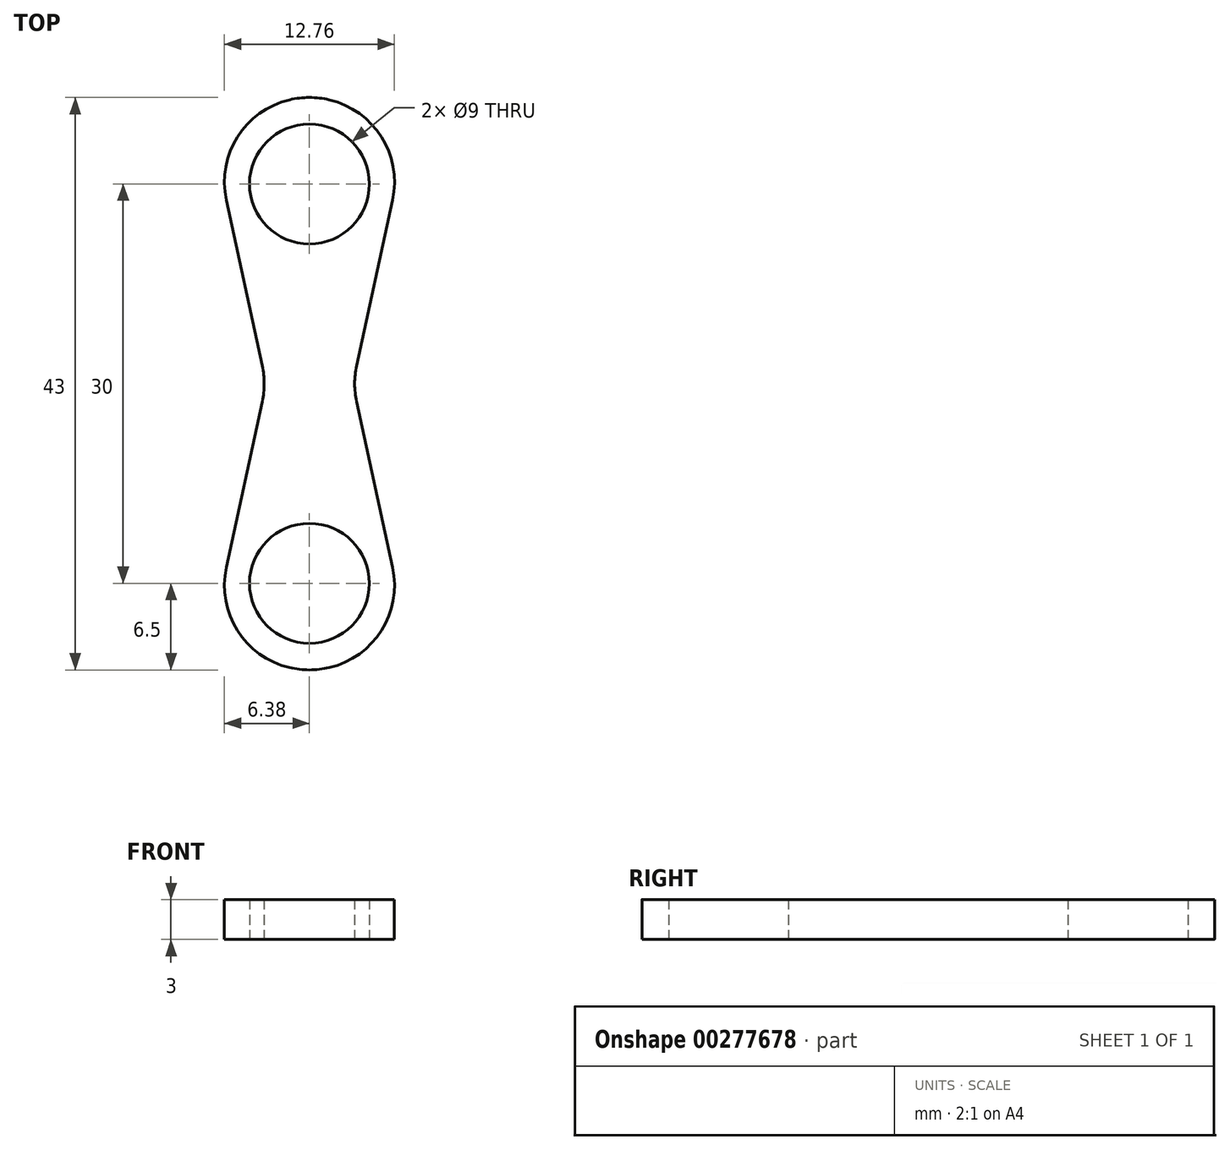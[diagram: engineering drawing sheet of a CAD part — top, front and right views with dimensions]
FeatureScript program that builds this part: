
annotation { "Feature Type Name" : "Feature", "Feature Type Description" : "" }
export const myFeature = defineFeature(function(context is Context, id is Id, definition is map)
    precondition{}
    {
        {
            var Q0;
            Q0=qCreatedBy(makeId("Top.planeOp"),FACE);
            var sketch = newSketch(context, id + "F0", { "sketchPlane" : qUnion([Q0])});
            skCircle(sketch, "E0", {"center": v(0, 0) * mm, "radius": 4.5 * mm});
            skCircle(sketch, "E1", {"center": v(0, 30) * mm, "radius": 4.5 * mm});
            skArc(sketch, "E2", {"start": v(1.49, 36.33) * mm, "mid": v(0, 36.5) * mm, "end": v(-1.49, 36.33) * mm});
            skArc(sketch, "E3", {"start": v(-1.49, -6.33) * mm, "mid": v(0, -6.5) * mm, "end": v(1.49, -6.33) * mm});
            skLineSegment(sketch, "E4", {"start": v(-6.24, 28.8) * mm, "end": v(-3.54, 16.34) * mm});
            skLineSegment(sketch, "E5", {"start": v(6.24, 28.8) * mm, "end": v(3.54, 16.34) * mm});
            skLineSegment(sketch, "E6", {"start": v(-6.24, 1.2) * mm, "end": v(-3.54, 13.66) * mm});
            skLineSegment(sketch, "E7", {"start": v(3.54, 13.66) * mm, "end": v(6.24, 1.2) * mm});
            skArc(sketch, "E8.filletArc", {"start": v(-3.54, 13.66) * mm, "mid": v(-3.4, 15) * mm, "end": v(-3.54, 16.34) * mm});
            skArc(sketch, "E9.filletArc", {"start": v(3.54, 16.34) * mm, "mid": v(3.4, 15) * mm, "end": v(3.54, 13.66) * mm});
            skPoint(sketch, "E10.visualSharp", {"position": v(-6.5, 30) * mm});
            skArc(sketch, "E10.filletArc", {"start": v(-1.49, 36.33) * mm, "mid": v(-5.4, 33.54) * mm, "end": v(-6.24, 28.8) * mm});
            skPoint(sketch, "E11.visualSharp", {"position": v(6.5, 30) * mm});
            skArc(sketch, "E11.filletArc", {"start": v(6.24, 28.8) * mm, "mid": v(5.4, 33.54) * mm, "end": v(1.49, 36.33) * mm});
            skPoint(sketch, "E12.visualSharp", {"position": v(-6.5, 0) * mm});
            skArc(sketch, "E12.filletArc", {"start": v(-6.24, 1.2) * mm, "mid": v(-5.4, -3.54) * mm, "end": v(-1.49, -6.33) * mm});
            skPoint(sketch, "E13.visualSharp", {"position": v(6.5, 0) * mm});
            skArc(sketch, "E13.filletArc", {"start": v(1.49, -6.33) * mm, "mid": v(5.4, -3.54) * mm, "end": v(6.24, 1.2) * mm});
            skSolve(sketch);
        }
        {
            var Q0;
            Q0=makeQuery(id+"F0.imprint","IMPRINT",FACE,{"disambiguationData":[TD([[makeQuery(id+"F0.imprint","IMPRINT",EDGE,{"derivedFrom":sQuery(id+"F0.wireOp",EDGE,"E0")}),-1.0]])]});
            extrude(context, id + "F1", {"entities" : qUnion([Q0]), "depth" : 3 * mm});
        }
    });
